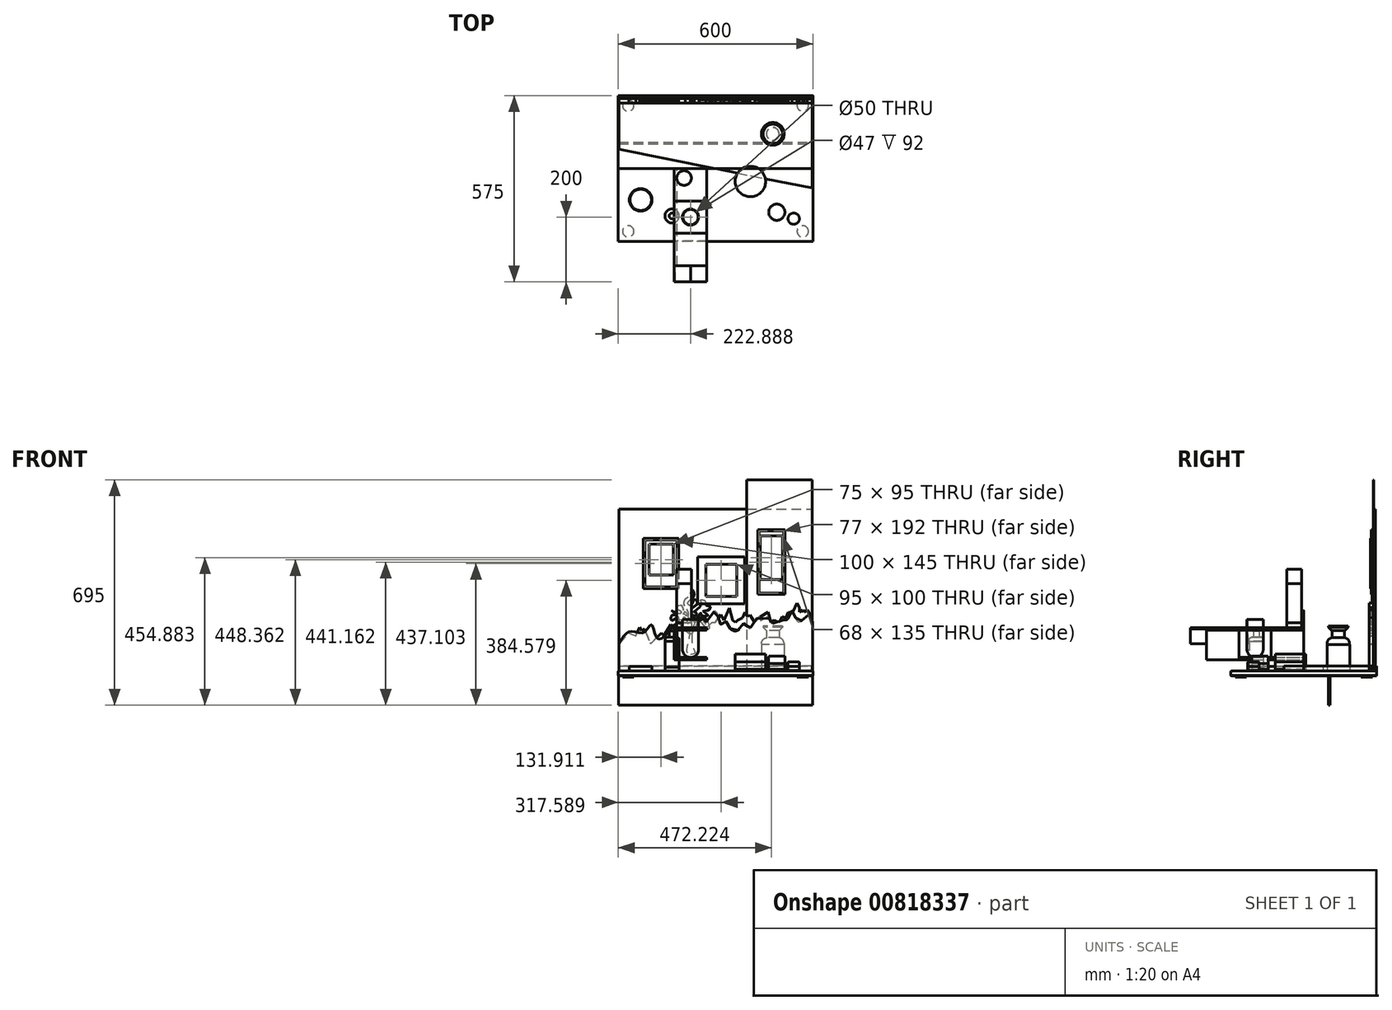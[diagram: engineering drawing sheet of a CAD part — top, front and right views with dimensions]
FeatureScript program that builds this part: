
annotation { "Feature Type Name" : "Feature", "Feature Type Description" : "" }
export const myFeature = defineFeature(function(context is Context, id is Id, definition is map)
    precondition{}
    {
        {
            var Q0;
            Q0=qCreatedBy(makeId("Top.planeOp"),FACE);
            var sketch = newSketch(context, id + "F0", { "sketchPlane" : qUnion([Q0])});
            skLineSegment(sketch, "E0.bottom", {"start": v(300, -225) * mm, "end": v(-300, -225) * mm});
            skLineSegment(sketch, "E0.top", {"start": v(300, 225) * mm, "end": v(-300, 225) * mm});
            skLineSegment(sketch, "E0.left", {"start": v(300, -225) * mm, "end": v(300, 225) * mm});
            skLineSegment(sketch, "E0.right", {"start": v(-300, -225) * mm, "end": v(-300, 225) * mm});
            skPoint(sketch, "E0.middle", {"position": v(0, 0) * mm});
            skSolve(sketch);
        }
        {
            var Q0;
            Q0=makeQuery(id+"F0.imprint","IMPRINT",FACE,{"disambiguationData":[TD([[makeQuery(id+"F0.imprint","IMPRINT",EDGE,{"derivedFrom":sQuery(id+"F0.wireOp",EDGE,"E0.bottom")}),-1.0]])]});
            extrude(context, id + "F1", {"entities" : qUnion([Q0]), "depth" : 15 * mm, "offsetDistance" : 25 * mm});
        }
        {
            var Q0;
            Q0=makeQuery(id+"F1.opExtrude","CAP_EDGE",EDGE,{"disambiguationData":[OSD([sQuery(id+"F0.wireOp",EDGE,"E0.bottom")])],"isStart":false});
            var Q1;
            Q1=makeQuery(id+"F1.opExtrude","CAP_EDGE",EDGE,{"disambiguationData":[OSD([sQuery(id+"F0.wireOp",EDGE,"E0.right")])],"isStart":false});
            var Q2;
            Q2=makeQuery(id+"F1.opExtrude","CAP_EDGE",EDGE,{"disambiguationData":[OSD([sQuery(id+"F0.wireOp",EDGE,"E0.left")])],"isStart":false});
            fillet(context, id + "F2", {"entities" : qUnion([Q0, Q1, Q2]), "radius" : 2 * mm, "tangentPropagation" : true, "allowEdgeOverflow" : false});
        }
        {
            var Q0;
            Q0=makeQuery(id+"F1.opExtrude","CAP_EDGE",EDGE,{"disambiguationData":[OSD([sQuery(id+"F0.wireOp",EDGE,"E0.right")])],"isStart":true});
            var Q1;
            Q1=makeQuery(id+"F1.opExtrude","CAP_EDGE",EDGE,{"disambiguationData":[OSD([sQuery(id+"F0.wireOp",EDGE,"E0.bottom")])],"isStart":true});
            var Q2;
            Q2=makeQuery(id+"F1.opExtrude","CAP_EDGE",EDGE,{"disambiguationData":[OSD([sQuery(id+"F0.wireOp",EDGE,"E0.left")])],"isStart":true});
            chamfer(context, id + "F3", {"entities" : qUnion([Q0, Q1, Q2]), "width" : 1 * mm, "tangentPropagation" : true});
        }
        {
            var Q0;
            Q0=makeQuery(id+"F1.opExtrude","CAP_FACE",FACE,{"disambiguationData":[OSD([sQuery(id+"F0.wireOp",EDGE,"E0.bottom"),sQuery(id+"F0.wireOp",EDGE,"E0.top"),sQuery(id+"F0.wireOp",EDGE,"E0.left"),sQuery(id+"F0.wireOp",EDGE,"E0.right")])],"isStart":false});
            var sketch = newSketch(context, id + "F4", { "sketchPlane" : qUnion([Q0])});
            skLineSegment(sketch, "E1.bottom", {"start": v(-298, 225) * mm, "end": v(298, 225) * mm});
            skLineSegment(sketch, "E1.top", {"start": v(-298, 210) * mm, "end": v(298, 210) * mm});
            skLineSegment(sketch, "E1.left", {"start": v(-298, 225) * mm, "end": v(-298, 210) * mm});
            skLineSegment(sketch, "E1.right", {"start": v(298, 225) * mm, "end": v(298, 210) * mm});
            skSolve(sketch);
        }
        {
            var Q0;
            Q0 = qSketchRegion(id + "F4", true);
            extrude(context, id + "F5", {"entities" : qUnion([Q0]), "depth" : 15 * mm, "offsetDistance" : 25 * mm});
        }
        {
            var Q0;
            Q0=makeQuery(id+"F5.opExtrude","CAP_EDGE",EDGE,{"disambiguationData":[OSD([sQuery(id+"F4.wireOp",EDGE,"E1.top")])],"isStart":false});
            fillet(context, id + "F6", {"entities" : qUnion([Q0]), "radius" : 10 * mm, "tangentPropagation" : true, "allowEdgeOverflow" : false});
        }
        {
            var Q0;
            Q0=makeQuery(id+"F1.opExtrude","CAP_FACE",FACE,{"disambiguationData":[OSD([sQuery(id+"F0.wireOp",EDGE,"E0.bottom"),sQuery(id+"F0.wireOp",EDGE,"E0.top"),sQuery(id+"F0.wireOp",EDGE,"E0.left"),sQuery(id+"F0.wireOp",EDGE,"E0.right")])],"isStart":false});
            var sketch = newSketch(context, id + "F7", { "sketchPlane" : qUnion([Q0])});
            skLineSegment(sketch, "E2.bottom", {"start": v(-298, 221.2) * mm, "end": v(298, 221.2) * mm});
            skLineSegment(sketch, "E2.top", {"start": v(-298, 216.2) * mm, "end": v(298, 216.2) * mm});
            skLineSegment(sketch, "E2.left", {"start": v(-298, 221.2) * mm, "end": v(-298, 216.2) * mm});
            skLineSegment(sketch, "E2.right", {"start": v(298, 221.2) * mm, "end": v(298, 216.2) * mm});
            skSolve(sketch);
        }
        {
            var Q0;
            Q0 = qSketchRegion(id + "F7", true);
            extrude(context, id + "F8", {"entities" : qUnion([Q0]), "depth" : 500 * mm, "offsetDistance" : 25 * mm});
        }
        {
            var Q0;
            Q0=qCreatedBy(makeId("Front.planeOp"),FACE);
            var sketch = newSketch(context, id + "F9", { "sketchPlane" : qUnion([Q0])});
            skLineSegment(sketch, "E3", {"start": v(-27.11, 49) * mm, "end": v(-127.11, 49) * mm});
            skLineSegment(sketch, "E4", {"start": v(-127.11, 49) * mm, "end": v(-127.11, 149) * mm});
            skLineSegment(sketch, "E5", {"start": v(-127.11, 149) * mm, "end": v(-27.11, 149) * mm});
            skLineSegment(sketch, "E6", {"start": v(-27.11, 149) * mm, "end": v(-27.11, 141) * mm});
            skLineSegment(sketch, "E7", {"start": v(-27.11, 141) * mm, "end": v(-119.11, 141) * mm});
            skLineSegment(sketch, "E8", {"start": v(-119.11, 141) * mm, "end": v(-119.11, 57) * mm});
            skLineSegment(sketch, "E9", {"start": v(-119.11, 57) * mm, "end": v(-27.11, 57) * mm});
            skLineSegment(sketch, "E10", {"start": v(-27.11, 57) * mm, "end": v(-27.11, 49) * mm});
            skSolve(sketch);
        }
        {
            var Q0;
            Q0 = qSketchRegion(id + "F9", true);
            extrude(context, id + "F10", {"entities" : qUnion([Q0]), "depth" : 100 * mm, "offsetDistance" : 25 * mm});
        }
        {
            var Q0;
            Q0=qCreatedBy(makeId("Front.planeOp"),FACE);
            var sketch = newSketch(context, id + "F11", { "sketchPlane" : qUnion([Q0])});
            skFitSpline(sketch, "E11", {"points": [v(-297.92, 99.43) * mm, v(-262.77, 137.05) * mm, v(-219.84, 134.73) * mm, v(-196.64, 157.93) * mm, v(-176.92, 113.85) * mm, v(-125.87, 157.93) * mm, v(-110.8, 160.25) * mm, v(-78.3, 130.1) * mm, v(-59.75, 154.45) * mm, v(-41.18, 179.98) * mm, v(-33.06, 163.73) * mm, v(0, 200.86) * mm, v(13.34, 159.1) * mm, v(30.74, 168.37) * mm, v(44.66, 146.33) * mm, v(72.5, 142.85) * mm, v(91.07, 163.73) * mm, v(103.83, 145.17) * mm, v(114.27, 160.25) * mm, v(137.47, 183.46) * mm, v(138.63, 170.7) * mm, v(158.36, 183.46) * mm, v(171.12, 163.73) * mm, v(207.08, 171.86) * mm, v(222.16, 175.34) * mm, v(237.24, 200.86) * mm, v(255.8, 166.05) * mm, v(284.8, 188.1) * mm, v(298.73, 169.54) * mm], "startDerivative": vector(635.3, 1148.27) * mm, "endDerivative": vector(359.34, -998.44) * mm});
            skLineSegment(sketch, "E12", {"start": v(298.73, 169.54) * mm, "end": v(298.73, 14.08) * mm});
            skLineSegment(sketch, "E13", {"start": v(298.73, 14.08) * mm, "end": v(-297.57, 14.08) * mm});
            skLineSegment(sketch, "E14", {"start": v(-297.57, 14.08) * mm, "end": v(-297.92, 99.43) * mm});
            skSolve(sketch);
        }
        {
            var Q0;
            Q0=makeQuery(id+"F11.imprint","IMPRINT",FACE,{"disambiguationData":[TD([[makeQuery(id+"F11.imprint","IMPRINT",EDGE,{"derivedFrom":sQuery(id+"F11.wireOp",EDGE,"E11")}),-1.0]])]});
            extrude(context, id + "F12", {"entities" : qUnion([Q0]), "depth" : .5 * mm, "offsetDistance" : 25 * mm});
        }
        {
            var Q0;
            Q0=makeQuery(id+"F1.opExtrude","CAP_FACE",FACE,{"disambiguationData":[OSD([sQuery(id+"F0.wireOp",EDGE,"E0.bottom"),sQuery(id+"F0.wireOp",EDGE,"E0.top"),sQuery(id+"F0.wireOp",EDGE,"E0.left"),sQuery(id+"F0.wireOp",EDGE,"E0.right")])],"isStart":true});
            var sketch = newSketch(context, id + "F13", { "sketchPlane" : qUnion([Q0])});
            skLineSegment(sketch, "E15.bottom", {"start": v(-299, -75.96) * mm, "end": v(299, -75.96) * mm});
            skLineSegment(sketch, "E15.top", {"start": v(-299, -80.96) * mm, "end": v(299, -80.96) * mm});
            skLineSegment(sketch, "E15.left", {"start": v(-299, -75.96) * mm, "end": v(-299, -80.96) * mm});
            skLineSegment(sketch, "E15.right", {"start": v(299, -75.96) * mm, "end": v(299, -80.96) * mm});
            skSolve(sketch);
        }
        {
            var Q0;
            Q0 = qSketchRegion(id + "F13", true);
            extrude(context, id + "F14", {"entities" : qUnion([Q0]), "depth" : 90 * mm, "offsetDistance" : 25 * mm});
        }
        {
            var Q0;
            Q0=makeQuery(id+"F1.opExtrude","CAP_FACE",FACE,{"disambiguationData":[OSD([sQuery(id+"F0.wireOp",EDGE,"E0.bottom"),sQuery(id+"F0.wireOp",EDGE,"E0.top"),sQuery(id+"F0.wireOp",EDGE,"E0.left"),sQuery(id+"F0.wireOp",EDGE,"E0.right")])],"isStart":false});
            var sketch = newSketch(context, id + "F15", { "sketchPlane" : qUnion([Q0])});
            skLineSegment(sketch, "E16.bottom", {"start": v(298, 216.34) * mm, "end": v(96, 216.34) * mm});
            skLineSegment(sketch, "E16.top", {"start": v(298, 214.13) * mm, "end": v(96, 214.13) * mm});
            skLineSegment(sketch, "E16.left", {"start": v(298, 216.34) * mm, "end": v(298, 214.13) * mm});
            skLineSegment(sketch, "E16.right", {"start": v(96, 216.34) * mm, "end": v(96, 214.13) * mm});
            skSolve(sketch);
        }
        {
            var Q0;
            Q0 = qSketchRegion(id + "F15", true);
            extrude(context, id + "F16", {"entities" : qUnion([Q0]), "depth" : 590 * mm, "offsetDistance" : 25 * mm});
        }
        {
            var Q0;
            Q0=makeQuery(id+"F10.opExtrude","SWEPT_FACE",FACE,{"disambiguationData":[OSD([sQuery(id+"F9.wireOp",EDGE,"E5")])]});
            var sketch = newSketch(context, id + "F17", { "sketchPlane" : qUnion([Q0])});
            skCircle(sketch, "E17", {"center": v(-96.89, -29.64) * mm, "radius": 22.5 * mm});
            skSolve(sketch);
        }
        {
            var Q0;
            Q0 = qSketchRegion(id + "F17", true);
            extrude(context, id + "F18", {"entities" : qUnion([Q0]), "depth" : 15 * mm, "offsetDistance" : 25 * mm});
        }
        {
            var Q0;
            Q0=makeQuery(id+"F18.opExtrude","CAP_FACE",FACE,{"disambiguationData":[OSD([sQuery(id+"F17.wireOp",EDGE,"E17")])],"isStart":false});
            var sketch = newSketch(context, id + "F19", { "sketchPlane" : qUnion([Q0])});
            skCircle(sketch, "E18", {"center": v(-96.89, -29.64) * mm, "radius": 22.5 * mm});
            skSolve(sketch);
        }
        {
            var Q0;
            Q0 = qSketchRegion(id + "F19", true);
            extrude(context, id + "F20", {"entities" : qUnion([Q0]), "depth" : 120 * mm, "offsetDistance" : 25 * mm});
        }
        {
            var Q0;
            Q0=makeQuery(id+"F20.opExtrude","CAP_FACE",FACE,{"disambiguationData":[OSD([sQuery(id+"F19.wireOp",EDGE,"E18")])],"isStart":false});
            var sketch = newSketch(context, id + "F21", { "sketchPlane" : qUnion([Q0])});
            skCircle(sketch, "E19", {"center": v(-96.89, -29.64) * mm, "radius": 22.5 * mm});
            skSolve(sketch);
        }
        {
            var Q0;
            Q0 = qSketchRegion(id + "F21", true);
            extrude(context, id + "F22", {"entities" : qUnion([Q0]), "depth" : 45 * mm, "offsetDistance" : 25 * mm});
        }
        {
            var Q0;
            Q0=makeQuery(id+"F1.opExtrude","CAP_FACE",FACE,{"disambiguationData":[OSD([sQuery(id+"F0.wireOp",EDGE,"E0.bottom"),sQuery(id+"F0.wireOp",EDGE,"E0.top"),sQuery(id+"F0.wireOp",EDGE,"E0.left"),sQuery(id+"F0.wireOp",EDGE,"E0.right")])],"isStart":false});
            var sketch = newSketch(context, id + "F23", { "sketchPlane" : qUnion([Q0])});
            skCircle(sketch, "E20", {"center": v(107.5, -40.26) * mm, "radius": 47 * mm});
            skSolve(sketch);
        }
        {
            var Q0;
            Q0 = qSketchRegion(id + "F23", true);
            extrude(context, id + "F24", {"entities" : qUnion([Q0]), "depth" : 6 * mm, "offsetDistance" : 25 * mm});
        }
        {
            var Q0;
            Q0=makeQuery(id+"F24.opExtrude","CAP_FACE",FACE,{"disambiguationData":[OSD([sQuery(id+"F23.wireOp",EDGE,"E20")])],"isStart":false});
            var sketch = newSketch(context, id + "F25", { "sketchPlane" : qUnion([Q0])});
            skCircle(sketch, "E21", {"center": v(107.5, -40.26) * mm, "radius": 47 * mm});
            skSolve(sketch);
        }
        {
            var Q0;
            Q0 = qSketchRegion(id + "F25", true);
            extrude(context, id + "F26", {"entities" : qUnion([Q0]), "depth" : 22 * mm, "offsetDistance" : 25 * mm});
        }
        {
            var Q0;
            Q0=makeQuery(id+"F26.opExtrude","CAP_FACE",FACE,{"disambiguationData":[OSD([sQuery(id+"F25.wireOp",EDGE,"E21")])],"isStart":false});
            var sketch = newSketch(context, id + "F27", { "sketchPlane" : qUnion([Q0])});
            skCircle(sketch, "E22", {"center": v(107.5, -40.26) * mm, "radius": 47 * mm});
            skSolve(sketch);
        }
        {
            var Q0;
            Q0 = qSketchRegion(id + "F27", true);
            extrude(context, id + "F28", {"entities" : qUnion([Q0]), "depth" : 24 * mm, "offsetDistance" : 25 * mm});
        }
        {
            var Q0;
            Q0=makeQuery(id+"F1.opExtrude","CAP_FACE",FACE,{"disambiguationData":[OSD([sQuery(id+"F0.wireOp",EDGE,"E0.bottom"),sQuery(id+"F0.wireOp",EDGE,"E0.top"),sQuery(id+"F0.wireOp",EDGE,"E0.left"),sQuery(id+"F0.wireOp",EDGE,"E0.right")])],"isStart":false});
            var sketch = newSketch(context, id + "F29", { "sketchPlane" : qUnion([Q0])});
            skCircle(sketch, "E23", {"center": v(176.52, 106.62) * mm, "radius": 35 * mm});
            skSolve(sketch);
        }
        {
            var Q0;
            Q0 = qSketchRegion(id + "F29", true);
            extrude(context, id + "F30", {"entities" : qUnion([Q0]), "depth" : 16 * mm, "offsetDistance" : 25 * mm});
        }
        {
            var Q0;
            Q0=makeQuery(id+"F30.opExtrude","CAP_FACE",FACE,{"disambiguationData":[OSD([sQuery(id+"F29.wireOp",EDGE,"E23")])],"isStart":false});
            var sketch = newSketch(context, id + "F31", { "sketchPlane" : qUnion([Q0])});
            skCircle(sketch, "E24", {"center": v(176.52, 106.62) * mm, "radius": 35 * mm});
            skSolve(sketch);
        }
        {
            var Q0;
            Q0 = qSketchRegion(id + "F31", true);
            extrude(context, id + "F32", {"entities" : qUnion([Q0]), "depth" : 65 * mm, "offsetDistance" : 25 * mm});
        }
        {
            var Q0;
            Q0=makeQuery(id+"F32.opExtrude","CAP_FACE",FACE,{"disambiguationData":[OSD([sQuery(id+"F31.wireOp",EDGE,"E24")])],"isStart":false});
            var sketch = newSketch(context, id + "F33", { "sketchPlane" : qUnion([Q0])});
            skCircle(sketch, "E25", {"center": v(176.52, 106.62) * mm, "radius": 34.57 * mm});
            skSolve(sketch);
        }
        {
            var Q0;
            Q0 = qSketchRegion(id + "F33", true);
            extrude(context, id + "F34", {"entities" : qUnion([Q0]), "depth" : 22 * mm, "offsetDistance" : 25 * mm});
        }
        {
            var Q0;
            Q0=makeQuery(id+"F34.opExtrude","CAP_EDGE",EDGE,{"disambiguationData":[OSD([sQuery(id+"F33.wireOp",EDGE,"E25")])],"isStart":false});
            fillet(context, id + "F35", {"entities" : qUnion([Q0]), "radius" : 18 * mm, "tangentPropagation" : true, "allowEdgeOverflow" : false});
        }
        {
            var Q0;
            Q0=makeQuery(id+"F34.opExtrude","CAP_FACE",FACE,{"disambiguationData":[OSD([sQuery(id+"F33.wireOp",EDGE,"E25")])],"isStart":false});
            var sketch = newSketch(context, id + "F36", { "sketchPlane" : qUnion([Q0])});
            skCircle(sketch, "E26", {"center": v(176.52, 106.62) * mm, "radius": 19.32 * mm});
            skSolve(sketch);
        }
        {
            var Q0;
            Q0 = qSketchRegion(id + "F36", true);
            extrude(context, id + "F37", {"entities" : qUnion([Q0]), "depth" : 22 * mm, "offsetDistance" : 25 * mm});
        }
        {
            var Q0;
            Q0=makeQuery(id+"F37.opExtrude","CAP_FACE",FACE,{"disambiguationData":[OSD([sQuery(id+"F36.wireOp",EDGE,"E26")])],"isStart":false});
            var sketch = newSketch(context, id + "F38", { "sketchPlane" : qUnion([Q0])});
            skCircle(sketch, "E27", {"center": v(176.52, 106.62) * mm, "radius": 30 * mm});
            skSolve(sketch);
        }
        {
            var Q0;
            Q0 = qSketchRegion(id + "F38", true);
            extrude(context, id + "F39", {"entities" : qUnion([Q0]), "operationType" : NewBodyOperationType.ADD, "depth" : 14 * mm, "offsetDistance" : 25 * mm});
        }
        {
            var Q0;
            Q0=makeQuery(id+"F39.opExtrude","CAP_EDGE",EDGE,{"disambiguationData":[OSD([sQuery(id+"F38.wireOp",EDGE,"E27")])],"isStart":true});
            chamfer(context, id + "F40", {"entities" : qUnion([Q0]), "width" : 10 * mm, "tangentPropagation" : true});
        }
        {
            var Q0;
            Q0=makeQuery(id+"F1.opExtrude","CAP_FACE",FACE,{"disambiguationData":[OSD([sQuery(id+"F0.wireOp",EDGE,"E0.bottom"),sQuery(id+"F0.wireOp",EDGE,"E0.top"),sQuery(id+"F0.wireOp",EDGE,"E0.left"),sQuery(id+"F0.wireOp",EDGE,"E0.right")])],"isStart":false});
            var sketch = newSketch(context, id + "F41", { "sketchPlane" : qUnion([Q0])});
            skCircle(sketch, "E28", {"center": v(-230.5, -96.89) * mm, "radius": 35 * mm});
            skSolve(sketch);
        }
        {
            var Q0;
            Q0 = qSketchRegion(id + "F41", true);
            extrude(context, id + "F42", {"entities" : qUnion([Q0]), "depth" : 14 * mm, "offsetDistance" : 25 * mm});
        }
        {
            var Q0;
            Q0=makeQuery(id+"F42.opExtrude","CAP_EDGE",EDGE,{"disambiguationData":[OSD([sQuery(id+"F41.wireOp",EDGE,"E28")])],"isStart":false});
            fillet(context, id + "F43", {"entities" : qUnion([Q0]), "radius" : 2 * mm, "tangentPropagation" : true, "allowEdgeOverflow" : false});
        }
        {
            var Q0;
            Q0=makeQuery(id+"F42.opExtrude","CAP_FACE",FACE,{"disambiguationData":[OSD([sQuery(id+"F41.wireOp",EDGE,"E28")])],"isStart":false});
            extrude(context, id + "F44", {"entities" : qUnion([Q0]), "depth" : .1 * mm, "offsetDistance" : 25 * mm});
        }
        {
            var Q0;
            Q0=makeQuery(id+"F1.opExtrude","CAP_FACE",FACE,{"disambiguationData":[OSD([sQuery(id+"F0.wireOp",EDGE,"E0.bottom"),sQuery(id+"F0.wireOp",EDGE,"E0.top"),sQuery(id+"F0.wireOp",EDGE,"E0.left"),sQuery(id+"F0.wireOp",EDGE,"E0.right")])],"isStart":false});
            var sketch = newSketch(context, id + "F45", { "sketchPlane" : qUnion([Q0])});
            skCircle(sketch, "E29", {"center": v(-134.05, -146.44) * mm, "radius": 21.5 * mm});
            skSolve(sketch);
        }
        {
            var Q0;
            Q0 = qSketchRegion(id + "F45", true);
            extrude(context, id + "F46", {"entities" : qUnion([Q0]), "depth" : 12 * mm, "offsetDistance" : 25 * mm});
        }
        {
            var Q0;
            Q0=makeQuery(id+"F46.opExtrude","CAP_FACE",FACE,{"disambiguationData":[OSD([sQuery(id+"F45.wireOp",EDGE,"E29")])],"isStart":false});
            var sketch = newSketch(context, id + "F47", { "sketchPlane" : qUnion([Q0])});
            skCircle(sketch, "E30", {"center": v(-134.05, -146.44) * mm, "radius": 21.5 * mm});
            skSolve(sketch);
        }
        {
            var Q0;
            Q0 = qSketchRegion(id + "F47", true);
            extrude(context, id + "F48", {"entities" : qUnion([Q0]), "depth" : 80 * mm, "offsetDistance" : 25 * mm});
        }
        {
            var Q0;
            Q0=makeQuery(id+"F48.opExtrude","CAP_FACE",FACE,{"disambiguationData":[OSD([sQuery(id+"F47.wireOp",EDGE,"E30")])],"isStart":false});
            var sketch = newSketch(context, id + "F49", { "sketchPlane" : qUnion([Q0])});
            skCircle(sketch, "E31", {"center": v(-134.05, -146.44) * mm, "radius": 22 * mm});
            skSolve(sketch);
        }
        {
            var Q0;
            Q0 = qSketchRegion(id + "F49", true);
            extrude(context, id + "F50", {"entities" : qUnion([Q0]), "depth" : 12 * mm, "offsetDistance" : 25 * mm});
        }
        {
            var Q0;
            Q0=makeQuery(id+"F50.opExtrude","CAP_EDGE",EDGE,{"disambiguationData":[OSD([sQuery(id+"F49.wireOp",EDGE,"E31")])],"isStart":false});
            fillet(context, id + "F51", {"entities" : qUnion([Q0]), "radius" : 7 * mm, "tangentPropagation" : true, "allowEdgeOverflow" : false});
        }
        {
            var Q0;
            Q0=makeQuery(id+"F50.opExtrude","CAP_FACE",FACE,{"disambiguationData":[OSD([sQuery(id+"F49.wireOp",EDGE,"E31")])],"isStart":false});
            var sketch = newSketch(context, id + "F52", { "sketchPlane" : qUnion([Q0])});
            skCircle(sketch, "E32", {"center": v(-134.05, -146.44) * mm, "radius": 8.77 * mm});
            skSolve(sketch);
        }
        {
            var Q0;
            Q0 = qSketchRegion(id + "F52", true);
            extrude(context, id + "F53", {"entities" : qUnion([Q0]), "operationType" : NewBodyOperationType.ADD, "depth" : 20 * mm, "offsetDistance" : 25 * mm});
        }
        {
            var Q0;
            Q0=makeQuery(id+"F53.opExtrude","CAP_EDGE",EDGE,{"disambiguationData":[OSD([sQuery(id+"F52.wireOp",EDGE,"E32")])],"isStart":false});
            fillet(context, id + "F54", {"entities" : qUnion([Q0]), "radius" : 3 * mm, "tangentPropagation" : true, "allowEdgeOverflow" : false});
        }
        {
            var Q0;
            Q0=makeQuery(id+"F10.opExtrude","CAP_FACE",FACE,{"disambiguationData":[OSD([sQuery(id+"F9.wireOp",EDGE,"E3"),sQuery(id+"F9.wireOp",EDGE,"E4"),sQuery(id+"F9.wireOp",EDGE,"E5"),sQuery(id+"F9.wireOp",EDGE,"E6"),sQuery(id+"F9.wireOp",EDGE,"E7"),sQuery(id+"F9.wireOp",EDGE,"E8"),sQuery(id+"F9.wireOp",EDGE,"E9"),sQuery(id+"F9.wireOp",EDGE,"E10")])],"isStart":false});
            var sketch = newSketch(context, id + "F55", { "sketchPlane" : qUnion([Q0])});
            skLineSegment(sketch, "E33", {"start": v(-27.11, 149) * mm, "end": v(-27.11, 141) * mm});
            skLineSegment(sketch, "E34", {"start": v(-27.11, 141) * mm, "end": v(-119.11, 141) * mm});
            skLineSegment(sketch, "E35", {"start": v(-119.11, 141) * mm, "end": v(-119.11, 57) * mm});
            skLineSegment(sketch, "E36", {"start": v(-119.11, 57) * mm, "end": v(-27.11, 57) * mm});
            skLineSegment(sketch, "E37", {"start": v(-27.11, 57) * mm, "end": v(-27.11, 49) * mm});
            skLineSegment(sketch, "E38", {"start": v(-27.11, 49) * mm, "end": v(-127.11, 49) * mm});
            skLineSegment(sketch, "E39", {"start": v(-127.11, 49) * mm, "end": v(-127.11, 149) * mm});
            skLineSegment(sketch, "E40", {"start": v(-127.11, 149) * mm, "end": v(-27.11, 149) * mm});
            skSolve(sketch);
        }
        {
            var Q0;
            Q0 = qSketchRegion(id + "F55", true);
            extrude(context, id + "F56", {"entities" : qUnion([Q0]), "depth" : 100 * mm, "offsetDistance" : 25 * mm});
        }
        {
            var Q0;
            Q0=makeQuery(id+"F56.opExtrude","SWEPT_FACE",FACE,{"disambiguationData":[OSD([sQuery(id+"F55.wireOp",EDGE,"E40")])]});
            var sketch = newSketch(context, id + "F57", { "sketchPlane" : qUnion([Q0])});
            skCircle(sketch, "E41", {"center": v(-77.11, -150) * mm, "radius": 25 * mm});
            skPoint(sketch, "E41.centerSnap0", {"position": v(-27.11, -150) * mm});
            skPoint(sketch, "E41.centerSnap1", {"position": v(-77.11, -100) * mm});
            skSolve(sketch);
        }
        {
            var Q0;
            Q0 = qSketchRegion(id + "F57", true);
            extrude(context, id + "F58", {"entities" : qUnion([Q0]), "oppositeDirection" : true, "depth" : 10 * mm, "offsetDistance" : 25 * mm});
        }
        {
            var Q0;
            Q0=makeQuery(id+"F58.opExtrude","SWEPT_BODY",BODY,{"disambiguationData":[OSD([sQuery(id+"F57.wireOp",EDGE,"E41")])]});
            var Q1;
            Q1=makeQuery(id+"F56.opExtrude","SWEPT_BODY",BODY,{"disambiguationData":[OSD([sQuery(id+"F55.wireOp",EDGE,"E33"),sQuery(id+"F55.wireOp",EDGE,"E34"),sQuery(id+"F55.wireOp",EDGE,"E35"),sQuery(id+"F55.wireOp",EDGE,"E36"),sQuery(id+"F55.wireOp",EDGE,"E37"),sQuery(id+"F55.wireOp",EDGE,"E38"),sQuery(id+"F55.wireOp",EDGE,"E39"),sQuery(id+"F55.wireOp",EDGE,"E40")])]});
            booleanBodies(context, id + "F59", {"operationType" : BooleanOperationType.SUBTRACTION, "tools" : qUnion([Q0]), "targets" : qUnion([Q1])});
        }
        {
            var Q0;
            Q0=makeQuery(id+"F56.opExtrude","SWEPT_FACE",FACE,{"disambiguationData":[OSD([sQuery(id+"F55.wireOp",EDGE,"E40")])]});
            var sketch = newSketch(context, id + "F60", { "sketchPlane" : qUnion([Q0])});
            skCircle(sketch, "E42", {"center": v(-77.11, -150) * mm, "radius": 25 * mm});
            skSolve(sketch);
        }
        {
            var Q0;
            Q0 = qSketchRegion(id + "F60", true);
            extrude(context, id + "F61", {"entities" : qUnion([Q0]), "depth" : 25 * mm, "offsetDistance" : 25 * mm, "hasSecondDirection" : true, "secondDirectionOppositeDirection" : true, "secondDirectionDepth" : 92 * mm});
        }
        {
            var Q0;
            Q0=makeQuery(id+"F61.opExtrude","CAP_EDGE",EDGE,{"disambiguationData":[OSD([sQuery(id+"F60.wireOp",EDGE,"E42")])],"isStart":true});
            fillet(context, id + "F62", {"entities" : qUnion([Q0]), "radius" : 25 * mm, "tangentPropagation" : true, "allowEdgeOverflow" : false});
        }
        {
            var Q0;
            Q0=makeQuery(id+"F61.opExtrude","CAP_FACE",FACE,{"disambiguationData":[OSD([sQuery(id+"F60.wireOp",EDGE,"E42")])],"isStart":false});
            shell(context, id + "F63", {"entities" : qUnion([Q0]), "thickness" : 1.5 * mm});
        }
        {
            var Q0;
            Q0=makeQuery(id+"F1.opExtrude","CAP_FACE",FACE,{"disambiguationData":[OSD([sQuery(id+"F0.wireOp",EDGE,"E0.bottom"),sQuery(id+"F0.wireOp",EDGE,"E0.top"),sQuery(id+"F0.wireOp",EDGE,"E0.left"),sQuery(id+"F0.wireOp",EDGE,"E0.right")])],"isStart":false});
            var sketch = newSketch(context, id + "F64", { "sketchPlane" : qUnion([Q0])});
            skCircle(sketch, "E43", {"center": v(188.91, -134.94) * mm, "radius": 25 * mm});
            skSolve(sketch);
        }
        {
            var Q0;
            Q0 = qSketchRegion(id + "F64", true);
            extrude(context, id + "F65", {"entities" : qUnion([Q0]), "depth" : 6 * mm, "offsetDistance" : 25 * mm});
        }
        {
            var Q0;
            Q0=makeQuery(id+"F65.opExtrude","CAP_FACE",FACE,{"disambiguationData":[OSD([sQuery(id+"F64.wireOp",EDGE,"E43")])],"isStart":false});
            var sketch = newSketch(context, id + "F66", { "sketchPlane" : qUnion([Q0])});
            skCircle(sketch, "E44", {"center": v(188.91, -134.94) * mm, "radius": 25 * mm});
            skSolve(sketch);
        }
        {
            var Q0;
            Q0 = qSketchRegion(id + "F66", true);
            extrude(context, id + "F67", {"entities" : qUnion([Q0]), "depth" : 17 * mm, "offsetDistance" : 25 * mm});
        }
        {
            var Q0;
            Q0=makeQuery(id+"F67.opExtrude","CAP_FACE",FACE,{"disambiguationData":[OSD([sQuery(id+"F66.wireOp",EDGE,"E44")])],"isStart":false});
            var sketch = newSketch(context, id + "F68", { "sketchPlane" : qUnion([Q0])});
            skCircle(sketch, "E45", {"center": v(188.91, -134.94) * mm, "radius": 25 * mm});
            skSolve(sketch);
        }
        {
            var Q0;
            Q0 = qSketchRegion(id + "F68", true);
            extrude(context, id + "F69", {"entities" : qUnion([Q0]), "depth" : 23 * mm, "offsetDistance" : 25 * mm});
        }
        {
            var Q0;
            Q0=makeQuery(id+"F69.opExtrude","CAP_EDGE",EDGE,{"disambiguationData":[OSD([sQuery(id+"F68.wireOp",EDGE,"E45")])],"isStart":false});
            fillet(context, id + "F70", {"entities" : qUnion([Q0]), "radius" : 3 * mm, "tangentPropagation" : true, "allowEdgeOverflow" : false});
        }
        {
            var Q0;
            Q0=makeQuery(id+"F1.opExtrude","CAP_FACE",FACE,{"disambiguationData":[OSD([sQuery(id+"F0.wireOp",EDGE,"E0.bottom"),sQuery(id+"F0.wireOp",EDGE,"E0.top"),sQuery(id+"F0.wireOp",EDGE,"E0.left"),sQuery(id+"F0.wireOp",EDGE,"E0.right")])],"isStart":false});
            var sketch = newSketch(context, id + "F71", { "sketchPlane" : qUnion([Q0])});
            skCircle(sketch, "E46", {"center": v(240.95, -154.96) * mm, "radius": 17.5 * mm});
            skSolve(sketch);
        }
        {
            var Q0;
            Q0 = qSketchRegion(id + "F71", true);
            extrude(context, id + "F72", {"entities" : qUnion([Q0]), "depth" : 2 * mm, "offsetDistance" : 25 * mm});
        }
        {
            var Q0;
            Q0=makeQuery(id+"F72.opExtrude","CAP_FACE",FACE,{"disambiguationData":[OSD([sQuery(id+"F71.wireOp",EDGE,"E46")])],"isStart":false});
            var sketch = newSketch(context, id + "F73", { "sketchPlane" : qUnion([Q0])});
            skCircle(sketch, "E47", {"center": v(240.95, -154.96) * mm, "radius": 17.5 * mm});
            skSolve(sketch);
        }
        {
            var Q0;
            Q0 = qSketchRegion(id + "F73", true);
            extrude(context, id + "F74", {"entities" : qUnion([Q0]), "depth" : 12 * mm, "offsetDistance" : 25 * mm});
        }
        {
            var Q0;
            Q0=makeQuery(id+"F74.opExtrude","CAP_FACE",FACE,{"disambiguationData":[OSD([sQuery(id+"F73.wireOp",EDGE,"E47")])],"isStart":false});
            var sketch = newSketch(context, id + "F75", { "sketchPlane" : qUnion([Q0])});
            skCircle(sketch, "E48", {"center": v(240.95, -154.96) * mm, "radius": 17.5 * mm});
            skSolve(sketch);
        }
        {
            var Q0;
            Q0 = qSketchRegion(id + "F75", true);
            extrude(context, id + "F76", {"entities" : qUnion([Q0]), "depth" : 14 * mm, "offsetDistance" : 25 * mm});
        }
        {
            var Q0;
            Q0=makeQuery(id+"F76.opExtrude","CAP_EDGE",EDGE,{"disambiguationData":[OSD([sQuery(id+"F75.wireOp",EDGE,"E48")])],"isStart":false});
            fillet(context, id + "F77", {"entities" : qUnion([Q0]), "radius" : 2 * mm, "tangentPropagation" : true, "allowEdgeOverflow" : false});
        }
        {
            var Q0;
            Q0=makeQuery(id+"F8.opExtrude","SWEPT_FACE",FACE,{"disambiguationData":[OSD([sQuery(id+"F7.wireOp",EDGE,"E2.top")])]});
            var sketch = newSketch(context, id + "F78", { "sketchPlane" : qUnion([Q0])});
            skLineSegment(sketch, "E49", {"start": v(-298, 98.3) * mm, "end": v(-267.17, 132.46) * mm});
            skLineSegment(sketch, "E50", {"start": v(-267.17, 132.46) * mm, "end": v(-246.16, 123.25) * mm});
            skLineSegment(sketch, "E51", {"start": v(-246.16, 123.25) * mm, "end": v(-234.44, 149.97) * mm});
            skLineSegment(sketch, "E52", {"start": v(-234.44, 149.97) * mm, "end": v(-227.22, 139.6) * mm});
            skLineSegment(sketch, "E53", {"start": v(-227.22, 139.6) * mm, "end": v(-219.18, 145.2) * mm});
            skLineSegment(sketch, "E54", {"start": v(-219.18, 145.2) * mm, "end": v(-200.53, 99.14) * mm});
            skLineSegment(sketch, "E55", {"start": v(-200.53, 99.14) * mm, "end": v(-166.96, 132.46) * mm});
            skLineSegment(sketch, "E56", {"start": v(-166.96, 132.46) * mm, "end": v(-159.39, 124.83) * mm});
            skLineSegment(sketch, "E57", {"start": v(-159.39, 124.83) * mm, "end": v(-137.69, 158.54) * mm});
            skLineSegment(sketch, "E58", {"start": v(-137.69, 158.54) * mm, "end": v(-124.42, 150) * mm});
            skLineSegment(sketch, "E59", {"start": v(-124.42, 150) * mm, "end": v(-92.93, 198.95) * mm});
            skLineSegment(sketch, "E60", {"start": v(-92.93, 198.95) * mm, "end": v(-77.43, 167.15) * mm});
            skLineSegment(sketch, "E61", {"start": v(-77.43, 167.15) * mm, "end": v(-68.47, 171.52) * mm});
            skLineSegment(sketch, "E62", {"start": v(-68.47, 171.52) * mm, "end": v(-64.97, 164.35) * mm});
            skLineSegment(sketch, "E63", {"start": v(-64.97, 164.35) * mm, "end": v(-50.26, 171.52) * mm});
            skLineSegment(sketch, "E64", {"start": v(-50.26, 171.52) * mm, "end": v(-30.08, 147.35) * mm});
            skLineSegment(sketch, "E65", {"start": v(-30.08, 147.35) * mm, "end": v(-18.15, 157.31) * mm});
            skLineSegment(sketch, "E66", {"start": v(-18.15, 157.31) * mm, "end": v(-10.28, 164.57) * mm});
            skLineSegment(sketch, "E67", {"start": v(-10.28, 164.57) * mm, "end": v(0, 164.57) * mm});
            skLineSegment(sketch, "E68", {"start": v(0, 164.57) * mm, "end": v(16.4, 188.68) * mm});
            skLineSegment(sketch, "E69", {"start": v(16.4, 188.68) * mm, "end": v(26.74, 171.52) * mm});
            skLineSegment(sketch, "E70", {"start": v(26.74, 171.52) * mm, "end": v(43.1, 209.34) * mm});
            skLineSegment(sketch, "E71", {"start": v(43.1, 209.34) * mm, "end": v(53.43, 171.52) * mm});
            skLineSegment(sketch, "E72", {"start": v(53.43, 171.52) * mm, "end": v(62.04, 164.57) * mm});
            skLineSegment(sketch, "E73", {"start": v(62.04, 164.57) * mm, "end": v(67.64, 171.52) * mm});
            skLineSegment(sketch, "E74", {"start": v(67.64, 171.52) * mm, "end": v(83.56, 179.2) * mm});
            skLineSegment(sketch, "E75", {"start": v(83.56, 179.2) * mm, "end": v(90.45, 197.28) * mm});
            skLineSegment(sketch, "E76", {"start": v(90.45, 197.28) * mm, "end": v(99.05, 183.5) * mm});
            skLineSegment(sketch, "E77", {"start": v(99.05, 183.5) * mm, "end": v(106.56, 188.2) * mm});
            skLineSegment(sketch, "E78", {"start": v(106.56, 188.2) * mm, "end": v(121.33, 164.57) * mm});
            skLineSegment(sketch, "E79", {"start": v(121.33, 164.57) * mm, "end": v(139.52, 183.5) * mm});
            skLineSegment(sketch, "E80", {"start": v(139.52, 183.5) * mm, "end": v(148.96, 189.41) * mm});
            skLineSegment(sketch, "E81", {"start": v(148.96, 189.41) * mm, "end": v(161.56, 197.28) * mm});
            skLineSegment(sketch, "E82", {"start": v(161.56, 197.28) * mm, "end": v(170.5, 164.57) * mm});
            skLineSegment(sketch, "E83", {"start": v(170.5, 164.57) * mm, "end": v(181.63, 171.52) * mm});
            skLineSegment(sketch, "E84", {"start": v(181.63, 171.52) * mm, "end": v(197.2, 164.57) * mm});
            skLineSegment(sketch, "E85", {"start": v(197.2, 164.57) * mm, "end": v(205.65, 183.5) * mm});
            skLineSegment(sketch, "E86", {"start": v(205.65, 183.5) * mm, "end": v(216.23, 178.79) * mm});
            skLineSegment(sketch, "E87", {"start": v(216.23, 178.79) * mm, "end": v(224.48, 197.28) * mm});
            skLineSegment(sketch, "E88", {"start": v(224.48, 197.28) * mm, "end": v(235.96, 192.16) * mm});
            skLineSegment(sketch, "E89", {"start": v(235.96, 192.16) * mm, "end": v(250.47, 224.7) * mm});
            skLineSegment(sketch, "E90", {"start": v(250.47, 224.7) * mm, "end": v(259.05, 210.97) * mm});
            skLineSegment(sketch, "E91", {"start": v(259.05, 210.97) * mm, "end": v(259.05, 197.28) * mm});
            skLineSegment(sketch, "E92", {"start": v(259.05, 197.28) * mm, "end": v(268.58, 203.25) * mm});
            skLineSegment(sketch, "E93", {"start": v(268.58, 203.25) * mm, "end": v(272.3, 197.28) * mm});
            skLineSegment(sketch, "E94", {"start": v(272.3, 197.28) * mm, "end": v(282.37, 203.57) * mm});
            skLineSegment(sketch, "E95", {"start": v(282.37, 203.57) * mm, "end": v(298, 178.56) * mm});
            skLineSegment(sketch, "E96", {"start": v(298, 178.56) * mm, "end": v(298, 15) * mm});
            skLineSegment(sketch, "E97", {"start": v(298, 15) * mm, "end": v(-298, 15) * mm});
            skLineSegment(sketch, "E98", {"start": v(-298, 15) * mm, "end": v(-298, 98.3) * mm});
            skSolve(sketch);
        }
        {
            var Q0;
            Q0=makeQuery(id+"F78.imprint","IMPRINT",FACE,{"disambiguationData":[TD([[makeQuery(id+"F78.imprint","IMPRINT",EDGE,{"derivedFrom":sQuery(id+"F78.wireOp",EDGE,"E49")}),-1.0]])]});
            extrude(context, id + "F79", {"entities" : qUnion([Q0]), "depth" : 15 * mm, "offsetDistance" : 25 * mm});
        }
        {
            var Q0;
            Q0=makeQuery(id+"F1.opExtrude","CAP_FACE",FACE,{"disambiguationData":[OSD([sQuery(id+"F0.wireOp",EDGE,"E0.bottom"),sQuery(id+"F0.wireOp",EDGE,"E0.top"),sQuery(id+"F0.wireOp",EDGE,"E0.left"),sQuery(id+"F0.wireOp",EDGE,"E0.right")])],"isStart":false});
            var sketch = newSketch(context, id + "F80", { "sketchPlane" : qUnion([Q0])});
            skLineSegment(sketch, "E99", {"start": v(-298, 210.01) * mm, "end": v(-298, 59.73) * mm});
            skLineSegment(sketch, "E100", {"start": v(-298, 59.73) * mm, "end": v(298, -60.61) * mm});
            skLineSegment(sketch, "E101", {"start": v(298, -60.61) * mm, "end": v(298, 210.01) * mm});
            skLineSegment(sketch, "E102", {"start": v(298, 210.01) * mm, "end": v(-298, 210.01) * mm});
            skSolve(sketch);
        }
        {
            var Q0;
            Q0 = qSketchRegion(id + "F80", true);
            extrude(context, id + "F81", {"entities" : qUnion([Q0]), "depth" : 15 * mm, "offsetDistance" : 25 * mm});
        }
        {
            var Q0;
            Q0=makeQuery(id+"F8.opExtrude","SWEPT_FACE",FACE,{"disambiguationData":[OSD([sQuery(id+"F7.wireOp",EDGE,"E2.top")])]});
            var sketch = newSketch(context, id + "F82", { "sketchPlane" : qUnion([Q0])});
            skFitSpline(sketch, "E103", {"points": [v(-85.55, 70.3) * mm, v(-81.93, 110.12) * mm, v(-80.49, 144.87) * mm, v(-88.45, 171.65) * mm, v(-100.03, 180.34) * mm, v(-120.3, 162.96) * mm, v(-113.06, 181.06) * mm, v(-125.37, 175.27) * mm, v(-136.95, 173.1) * mm, v(-132.6, 187.58) * mm, v(-116.68, 188.3) * mm, v(-134.78, 200.6) * mm, v(-111.61, 192.64) * mm, v(-105.1, 197.71) * mm, v(-120.3, 207.85) * mm, v(-108, 218.7) * mm, v(-99.3, 204.23) * mm, v(-93.52, 187.58) * mm, v(-83.38, 186.85) * mm, v(-92.07, 212.91) * mm, v(-97.14, 221.6) * mm, v(-92.07, 238.25) * mm, v(-79.04, 249.1) * mm, v(-72.52, 265.76) * mm, v(-66, 254.18) * mm, v(-73.25, 237.53) * mm, v(-86.28, 223.77) * mm, v(-75.42, 218.7) * mm, v(-65.28, 235.35) * mm, v(-55.87, 224.5) * mm, v(-73.97, 206.4) * mm, v(-73.97, 189.75) * mm, v(-66.73, 185.4) * mm, v(-66, 179.61) * mm, v(-58.77, 194.82) * mm, v(-66.73, 196.99) * mm, v(-47.9, 213.64) * mm, v(-45.01, 229.56) * mm, v(-46.46, 233.9) * mm, v(-31.98, 231.01) * mm, v(-28.36, 217.26) * mm, v(-16.78, 215.09) * mm, v(-21.12, 202.78) * mm, v(-37.77, 199.16) * mm, v(-23.3, 186.13) * mm, v(-44.3, 187.58) * mm, v(-44.3, 194.1) * mm, v(-56.6, 178.89) * mm, v(-34.16, 180.34) * mm, v(-20.4, 144.14) * mm, v(-26.2, 149.2) * mm, v(-37.05, 170.93) * mm, v(-55.15, 176) * mm, v(-66.73, 157.9) * mm, v(-72.52, 131.11) * mm, v(-68.18, 84.78) * mm, v(-63.84, 69.58) * mm, v(-85.55, 70.3) * mm]});
            skSolve(sketch);
        }
        {
            var Q0;
            Q0 = qSketchRegion(id + "F82", true);
            extrude(context, id + "F83", {"entities" : qUnion([Q0]), "depth" : 1 * mm, "offsetDistance" : 25 * mm});
        }
        {
            var Q0;
            Q0=makeQuery(id+"F56.opExtrude","CAP_FACE",FACE,{"disambiguationData":[OSD([sQuery(id+"F55.wireOp",EDGE,"E33"),sQuery(id+"F55.wireOp",EDGE,"E34"),sQuery(id+"F55.wireOp",EDGE,"E35"),sQuery(id+"F55.wireOp",EDGE,"E36"),sQuery(id+"F55.wireOp",EDGE,"E37"),sQuery(id+"F55.wireOp",EDGE,"E38"),sQuery(id+"F55.wireOp",EDGE,"E39"),sQuery(id+"F55.wireOp",EDGE,"E40")])],"isStart":false});
            var sketch = newSketch(context, id + "F84", { "sketchPlane" : qUnion([Q0])});
            skLineSegment(sketch, "E104", {"start": v(-27.11, 149) * mm, "end": v(-127.11, 149) * mm});
            skLineSegment(sketch, "E105", {"start": v(-127.11, 149) * mm, "end": v(-127.11, 49) * mm});
            skLineSegment(sketch, "E106", {"start": v(-127.11, 49) * mm, "end": v(-119.11, 49) * mm});
            skLineSegment(sketch, "E107", {"start": v(-119.11, 49) * mm, "end": v(-119.11, 141) * mm});
            skLineSegment(sketch, "E108", {"start": v(-119.11, 141) * mm, "end": v(-27.11, 141) * mm});
            skLineSegment(sketch, "E109", {"start": v(-27.11, 141) * mm, "end": v(-27.11, 149) * mm});
            skSolve(sketch);
        }
        {
            var Q0;
            Q0 = qSketchRegion(id + "F84", true);
            extrude(context, id + "F85", {"entities" : qUnion([Q0]), "depth" : 100 * mm, "offsetDistance" : 25 * mm});
        }
        {
            var Q0;
            Q0=makeQuery(id+"F85.opExtrude","SWEPT_FACE",FACE,{"disambiguationData":[OSD([sQuery(id+"F84.wireOp",EDGE,"E104")])]});
            var sketch = newSketch(context, id + "F86", { "sketchPlane" : qUnion([Q0])});
            skLineSegment(sketch, "E110.bottom", {"start": v(-127.11, -200) * mm, "end": v(-27.11, -200) * mm});
            skLineSegment(sketch, "E110.top", {"start": v(-127.11, -300) * mm, "end": v(-27.11, -300) * mm});
            skLineSegment(sketch, "E110.left", {"start": v(-127.11, -200) * mm, "end": v(-127.11, -300) * mm});
            skLineSegment(sketch, "E110.right", {"start": v(-27.11, -200) * mm, "end": v(-27.11, -300) * mm});
            skSolve(sketch);
        }
        {
            var Q0;
            Q0 = qSketchRegion(id + "F86", true);
            extrude(context, id + "F87", {"entities" : qUnion([Q0]), "depth" : .1 * mm, "offsetDistance" : 25 * mm});
        }
        {
            var Q0;
            Q0=makeQuery(id+"F85.opExtrude","CAP_FACE",FACE,{"disambiguationData":[OSD([sQuery(id+"F84.wireOp",EDGE,"E104"),sQuery(id+"F84.wireOp",EDGE,"E105"),sQuery(id+"F84.wireOp",EDGE,"E106"),sQuery(id+"F84.wireOp",EDGE,"E107"),sQuery(id+"F84.wireOp",EDGE,"E108"),sQuery(id+"F84.wireOp",EDGE,"E109")])],"isStart":false});
            var sketch = newSketch(context, id + "F88", { "sketchPlane" : qUnion([Q0])});
            skLineSegment(sketch, "E111", {"start": v(-127.11, 149) * mm, "end": v(-77.11, 149) * mm});
            skLineSegment(sketch, "E112", {"start": v(-77.11, 149) * mm, "end": v(-77.11, 145) * mm});
            skLineSegment(sketch, "E113", {"start": v(-77.11, 145) * mm, "end": v(-123.11, 145) * mm});
            skLineSegment(sketch, "E114", {"start": v(-123.11, 145) * mm, "end": v(-123.11, 99) * mm});
            skLineSegment(sketch, "E115", {"start": v(-123.11, 99) * mm, "end": v(-127.11, 99) * mm});
            skLineSegment(sketch, "E116", {"start": v(-127.11, 99) * mm, "end": v(-127.11, 149) * mm});
            skSolve(sketch);
        }
        {
            var Q0;
            Q0 = qSketchRegion(id + "F88", true);
            extrude(context, id + "F89", {"entities" : qUnion([Q0]), "depth" : 50 * mm, "offsetDistance" : 25 * mm});
        }
        {
            var Q0;
            Q0=makeQuery(id+"F89.opExtrude","SWEPT_FACE",FACE,{"disambiguationData":[OSD([sQuery(id+"F88.wireOp",EDGE,"E111")])]});
            var sketch = newSketch(context, id + "F90", { "sketchPlane" : qUnion([Q0])});
            skLineSegment(sketch, "E117.bottom", {"start": v(-127.11, -300) * mm, "end": v(-77.11, -300) * mm});
            skLineSegment(sketch, "E117.top", {"start": v(-127.11, -350) * mm, "end": v(-77.11, -350) * mm});
            skLineSegment(sketch, "E117.left", {"start": v(-127.11, -300) * mm, "end": v(-127.11, -350) * mm});
            skLineSegment(sketch, "E117.right", {"start": v(-77.11, -300) * mm, "end": v(-77.11, -350) * mm});
            skSolve(sketch);
        }
        {
            var Q0;
            Q0 = qSketchRegion(id + "F90", true);
            extrude(context, id + "F91", {"entities" : qUnion([Q0]), "depth" : .1 * mm, "offsetDistance" : 25 * mm});
        }
        {
            var Q0;
            Q0=makeQuery(id+"F91.opExtrude","CAP_FACE",FACE,{"disambiguationData":[OSD([sQuery(id+"F90.wireOp",EDGE,"E117.bottom"),sQuery(id+"F90.wireOp",EDGE,"E117.top"),sQuery(id+"F90.wireOp",EDGE,"E117.left"),sQuery(id+"F90.wireOp",EDGE,"E117.right")])],"isStart":false});
            var sketch = newSketch(context, id + "F92", { "sketchPlane" : qUnion([Q0])});
            skLineSegment(sketch, "E118.bottom", {"start": v(-77.11, -300) * mm, "end": v(-27.11, -300) * mm});
            skLineSegment(sketch, "E118.top", {"start": v(-77.11, -350) * mm, "end": v(-27.11, -350) * mm});
            skLineSegment(sketch, "E118.left", {"start": v(-77.11, -300) * mm, "end": v(-77.11, -350) * mm});
            skLineSegment(sketch, "E118.right", {"start": v(-27.11, -300) * mm, "end": v(-27.11, -350) * mm});
            skSolve(sketch);
        }
        {
            var Q0;
            Q0 = qSketchRegion(id + "F92", true);
            extrude(context, id + "F93", {"entities" : qUnion([Q0]), "depth" : .1 * mm, "offsetDistance" : 25 * mm});
        }
        {
            var Q0;
            Q0=makeQuery(id+"F1.opExtrude","CAP_FACE",FACE,{"disambiguationData":[OSD([sQuery(id+"F0.wireOp",EDGE,"E0.bottom"),sQuery(id+"F0.wireOp",EDGE,"E0.top"),sQuery(id+"F0.wireOp",EDGE,"E0.left"),sQuery(id+"F0.wireOp",EDGE,"E0.right")])],"isStart":true});
            var sketch = newSketch(context, id + "F94", { "sketchPlane" : qUnion([Q0])});
            skCircle(sketch, "E119", {"center": v(269, 194) * mm, "radius": 17.5 * mm});
            skSolve(sketch);
        }
        {
            var Q0;
            Q0 = qSketchRegion(id + "F94", true);
            extrude(context, id + "F95", {"entities" : qUnion([Q0]), "depth" : 4 * mm, "offsetDistance" : 25 * mm});
        }
        {
            var Q0;
            Q0=makeQuery(id+"F95.opExtrude","SWEPT_BODY",BODY,{"disambiguationData":[OSD([sQuery(id+"F94.wireOp",EDGE,"E119")])]});
            var Q1;
            Q1=qCreatedBy(makeId("Right.planeOp"),FACE);
            mirror(context, id + "F96", {"entities" : qUnion([Q0]), "mirrorPlane" : qUnion([Q1])});
        }
        {
            var Q0;
            Q0=makeQuery(id+"F96.opPattern","COPY",BODY,{"derivedFrom":makeQuery(id+"F95.opExtrude","SWEPT_BODY",BODY,{"disambiguationData":[OSD([sQuery(id+"F94.wireOp",EDGE,"E119")])]}),"instanceName":"1"});
            var Q1;
            Q1=makeQuery(id+"F95.opExtrude","SWEPT_BODY",BODY,{"disambiguationData":[OSD([sQuery(id+"F94.wireOp",EDGE,"E119")])]});
            var Q2;
            Q2=qCreatedBy(makeId("Front.planeOp"),FACE);
            mirror(context, id + "F97", {"entities" : qUnion([Q0, Q1]), "mirrorPlane" : qUnion([Q2])});
        }
        {
            var Q0;
            Q0=makeQuery(id+"F8.opExtrude","SWEPT_FACE",FACE,{"disambiguationData":[OSD([sQuery(id+"F7.wireOp",EDGE,"E2.top")])]});
            var sketch = newSketch(context, id + "F98", { "sketchPlane" : qUnion([Q0])});
            skLineSegment(sketch, "E120.bottom", {"start": v(-223.09, 424.6) * mm, "end": v(-113.09, 424.6) * mm});
            skLineSegment(sketch, "E120.top", {"start": v(-223.09, 269.6) * mm, "end": v(-113.09, 269.6) * mm});
            skLineSegment(sketch, "E120.left", {"start": v(-223.09, 424.6) * mm, "end": v(-223.09, 269.6) * mm});
            skLineSegment(sketch, "E120.right", {"start": v(-113.09, 424.6) * mm, "end": v(-113.09, 269.6) * mm});
            skLineSegment(sketch, "E121.0", {"start": v(-218.09, 419.6) * mm, "end": v(-118.09, 419.6) * mm});
            skLineSegment(sketch, "E121.1", {"start": v(-218.09, 419.6) * mm, "end": v(-218.09, 274.6) * mm});
            skLineSegment(sketch, "E121.2", {"start": v(-218.09, 274.6) * mm, "end": v(-118.09, 274.6) * mm});
            skLineSegment(sketch, "E121.3", {"start": v(-118.09, 419.6) * mm, "end": v(-118.09, 274.6) * mm});
            skSolve(sketch);
        }
        {
            var Q0;
            Q0 = qSketchRegion(id + "F98", true);
            extrude(context, id + "F99", {"entities" : qUnion([Q0]), "depth" : 10 * mm, "offsetDistance" : 25 * mm});
        }
        {
            var Q0;
            Q0=makeQuery(id+"F8.opExtrude","SWEPT_FACE",FACE,{"disambiguationData":[OSD([sQuery(id+"F7.wireOp",EDGE,"E2.top")])]});
            var sketch = newSketch(context, id + "F100", { "sketchPlane" : qUnion([Q0])});
            skLineSegment(sketch, "E122.bottom", {"start": v(-218.09, 419.6) * mm, "end": v(-118.09, 419.6) * mm});
            skLineSegment(sketch, "E122.top", {"start": v(-218.09, 274.6) * mm, "end": v(-118.09, 274.6) * mm});
            skLineSegment(sketch, "E122.left", {"start": v(-218.09, 419.6) * mm, "end": v(-218.09, 274.6) * mm});
            skLineSegment(sketch, "E122.right", {"start": v(-118.09, 419.6) * mm, "end": v(-118.09, 274.6) * mm});
            skLineSegment(sketch, "E123.bottom", {"start": v(-205.59, 405.86) * mm, "end": v(-130.59, 405.86) * mm});
            skLineSegment(sketch, "E123.top", {"start": v(-205.59, 310.86) * mm, "end": v(-130.59, 310.86) * mm});
            skLineSegment(sketch, "E123.left", {"start": v(-205.59, 405.86) * mm, "end": v(-205.59, 310.86) * mm});
            skLineSegment(sketch, "E123.right", {"start": v(-130.59, 405.86) * mm, "end": v(-130.59, 310.86) * mm});
            skSolve(sketch);
        }
        {
            var Q0;
            Q0 = qSketchRegion(id + "F100", true);
            extrude(context, id + "F101", {"entities" : qUnion([Q0]), "depth" : 5 * mm, "offsetDistance" : 25 * mm});
        }
        {
            var Q0;
            Q0=makeQuery(id+"F8.opExtrude","SWEPT_FACE",FACE,{"disambiguationData":[OSD([sQuery(id+"F7.wireOp",EDGE,"E2.top")])]});
            var sketch = newSketch(context, id + "F102", { "sketchPlane" : qUnion([Q0])});
            skLineSegment(sketch, "E124.bottom", {"start": v(-54.91, 367.08) * mm, "end": v(90.09, 367.08) * mm});
            skLineSegment(sketch, "E124.top", {"start": v(-54.91, 222.08) * mm, "end": v(90.09, 222.08) * mm});
            skLineSegment(sketch, "E124.left", {"start": v(-54.91, 367.08) * mm, "end": v(-54.91, 222.08) * mm});
            skLineSegment(sketch, "E124.right", {"start": v(90.09, 367.08) * mm, "end": v(90.09, 222.08) * mm});
            skLineSegment(sketch, "E125.bottom", {"start": v(-29.91, 344.58) * mm, "end": v(65.09, 344.58) * mm});
            skLineSegment(sketch, "E125.top", {"start": v(-29.91, 244.58) * mm, "end": v(65.09, 244.58) * mm});
            skLineSegment(sketch, "E125.left", {"start": v(-29.91, 344.58) * mm, "end": v(-29.91, 244.58) * mm});
            skLineSegment(sketch, "E125.right", {"start": v(65.09, 344.58) * mm, "end": v(65.09, 244.58) * mm});
            skSolve(sketch);
        }
        {
            var Q0;
            Q0 = qSketchRegion(id + "F102", true);
            extrude(context, id + "F103", {"entities" : qUnion([Q0]), "depth" : 5 * mm, "offsetDistance" : 25 * mm});
        }
        {
            var Q0;
            Q0=makeQuery(id+"F8.opExtrude","SWEPT_FACE",FACE,{"disambiguationData":[OSD([sQuery(id+"F7.wireOp",EDGE,"E2.top")])]});
            var sketch = newSketch(context, id + "F104", { "sketchPlane" : qUnion([Q0])});
            skLineSegment(sketch, "E126.bottom", {"start": v(-205.59, 405.86) * mm, "end": v(-130.59, 405.86) * mm});
            skLineSegment(sketch, "E126.top", {"start": v(-205.59, 310.86) * mm, "end": v(-130.59, 310.86) * mm});
            skLineSegment(sketch, "E126.left", {"start": v(-205.59, 405.86) * mm, "end": v(-205.59, 310.86) * mm});
            skLineSegment(sketch, "E126.right", {"start": v(-130.59, 405.86) * mm, "end": v(-130.59, 310.86) * mm});
            skSolve(sketch);
        }
        {
            var Q0;
            Q0 = qSketchRegion(id + "F104", true);
            extrude(context, id + "F105", {"entities" : qUnion([Q0]), "depth" : 3 * mm, "offsetDistance" : 25 * mm});
        }
        {
            var Q0;
            Q0=makeQuery(id+"F8.opExtrude","SWEPT_FACE",FACE,{"disambiguationData":[OSD([sQuery(id+"F7.wireOp",EDGE,"E2.top")])]});
            var sketch = newSketch(context, id + "F106", { "sketchPlane" : qUnion([Q0])});
            skLineSegment(sketch, "E127.bottom", {"start": v(-29.91, 344.58) * mm, "end": v(65.09, 344.58) * mm});
            skLineSegment(sketch, "E127.top", {"start": v(-29.91, 244.58) * mm, "end": v(65.09, 244.58) * mm});
            skLineSegment(sketch, "E127.left", {"start": v(-29.91, 344.58) * mm, "end": v(-29.91, 244.58) * mm});
            skLineSegment(sketch, "E127.right", {"start": v(65.09, 344.58) * mm, "end": v(65.09, 244.58) * mm});
            skSolve(sketch);
        }
        {
            var Q0;
            Q0 = qSketchRegion(id + "F106", true);
            extrude(context, id + "F107", {"entities" : qUnion([Q0]), "depth" : 2 * mm, "offsetDistance" : 25 * mm});
        }
        {
            var Q0;
            Q0=makeQuery(id+"F8.opExtrude","SWEPT_FACE",FACE,{"disambiguationData":[OSD([sQuery(id+"F7.wireOp",EDGE,"E2.top")])]});
            var sketch = newSketch(context, id + "F108", { "sketchPlane" : qUnion([Q0])});
            skLineSegment(sketch, "E128.bottom", {"start": v(129.72, 451.16) * mm, "end": v(214.72, 451.16) * mm});
            skLineSegment(sketch, "E128.top", {"start": v(129.72, 251.16) * mm, "end": v(214.72, 251.16) * mm});
            skLineSegment(sketch, "E128.left", {"start": v(129.72, 451.16) * mm, "end": v(129.72, 251.16) * mm});
            skLineSegment(sketch, "E128.right", {"start": v(214.72, 451.16) * mm, "end": v(214.72, 251.16) * mm});
            skLineSegment(sketch, "E129.0", {"start": v(133.72, 447.16) * mm, "end": v(210.72, 447.16) * mm});
            skLineSegment(sketch, "E129.1", {"start": v(133.72, 447.16) * mm, "end": v(133.72, 255.16) * mm});
            skLineSegment(sketch, "E129.2", {"start": v(133.72, 255.16) * mm, "end": v(210.72, 255.16) * mm});
            skLineSegment(sketch, "E129.3", {"start": v(210.72, 447.16) * mm, "end": v(210.72, 255.16) * mm});
            skSolve(sketch);
        }
        {
            var Q0;
            Q0 = qSketchRegion(id + "F108", true);
            extrude(context, id + "F109", {"entities" : qUnion([Q0]), "depth" : 8 * mm, "offsetDistance" : 25 * mm});
        }
        {
            var Q0;
            {var subQ1=sQuery(id+"F7.wireOp",EDGE,"E2.left");var subQ2=sQuery(id+"F7.wireOp",EDGE,"E2.top");Q0=makeQuery(id+"F109.boolean.opBoolean","SPLIT",FACE,{"disambiguationData":[TD([makeQuery(id+"F8.opExtrude","SWEPT_FACE",FACE,{"disambiguationData":[OSD([subQ1])]})])],"derivedFrom":makeQuery(id+"F8.opExtrude","SWEPT_FACE",FACE,{"disambiguationData":[OSD([subQ2])]})});}
            var sketch = newSketch(context, id + "F110", { "sketchPlane" : qUnion([Q0])});
            skLineSegment(sketch, "E130.bottom", {"start": v(133.72, 447.16) * mm, "end": v(210.72, 447.16) * mm});
            skLineSegment(sketch, "E130.top", {"start": v(133.72, 255.16) * mm, "end": v(210.72, 255.16) * mm});
            skLineSegment(sketch, "E130.left", {"start": v(133.72, 447.16) * mm, "end": v(133.72, 255.16) * mm});
            skLineSegment(sketch, "E130.right", {"start": v(210.72, 447.16) * mm, "end": v(210.72, 255.16) * mm});
            skLineSegment(sketch, "E131.bottom", {"start": v(138.22, 432.38) * mm, "end": v(206.22, 432.38) * mm});
            skLineSegment(sketch, "E131.top", {"start": v(138.22, 297.38) * mm, "end": v(206.22, 297.38) * mm});
            skLineSegment(sketch, "E131.left", {"start": v(138.22, 432.38) * mm, "end": v(138.22, 297.38) * mm});
            skLineSegment(sketch, "E131.right", {"start": v(206.22, 432.38) * mm, "end": v(206.22, 297.38) * mm});
            skSolve(sketch);
        }
        {
            var Q0;
            Q0 = qSketchRegion(id + "F110", true);
            extrude(context, id + "F111", {"entities" : qUnion([Q0]), "depth" : 4 * mm, "offsetDistance" : 25 * mm});
        }
        {
            var Q0;
            Q0=makeQuery(id+"F8.opExtrude","SWEPT_FACE",FACE,{"disambiguationData":[OSD([sQuery(id+"F7.wireOp",EDGE,"E2.top")])]});
            var sketch = newSketch(context, id + "F112", { "sketchPlane" : qUnion([Q0])});
            skLineSegment(sketch, "E132.bottom", {"start": v(138.22, 432.38) * mm, "end": v(206.22, 432.38) * mm});
            skLineSegment(sketch, "E132.top", {"start": v(138.22, 297.38) * mm, "end": v(206.22, 297.38) * mm});
            skLineSegment(sketch, "E132.left", {"start": v(138.22, 432.38) * mm, "end": v(138.22, 297.38) * mm});
            skLineSegment(sketch, "E132.right", {"start": v(206.22, 432.38) * mm, "end": v(206.22, 297.38) * mm});
            skSolve(sketch);
        }
        {
            var Q0;
            Q0 = qSketchRegion(id + "F112", true);
            extrude(context, id + "F113", {"entities" : qUnion([Q0]), "depth" : 2 * mm, "offsetDistance" : 25 * mm});
        }
    });
